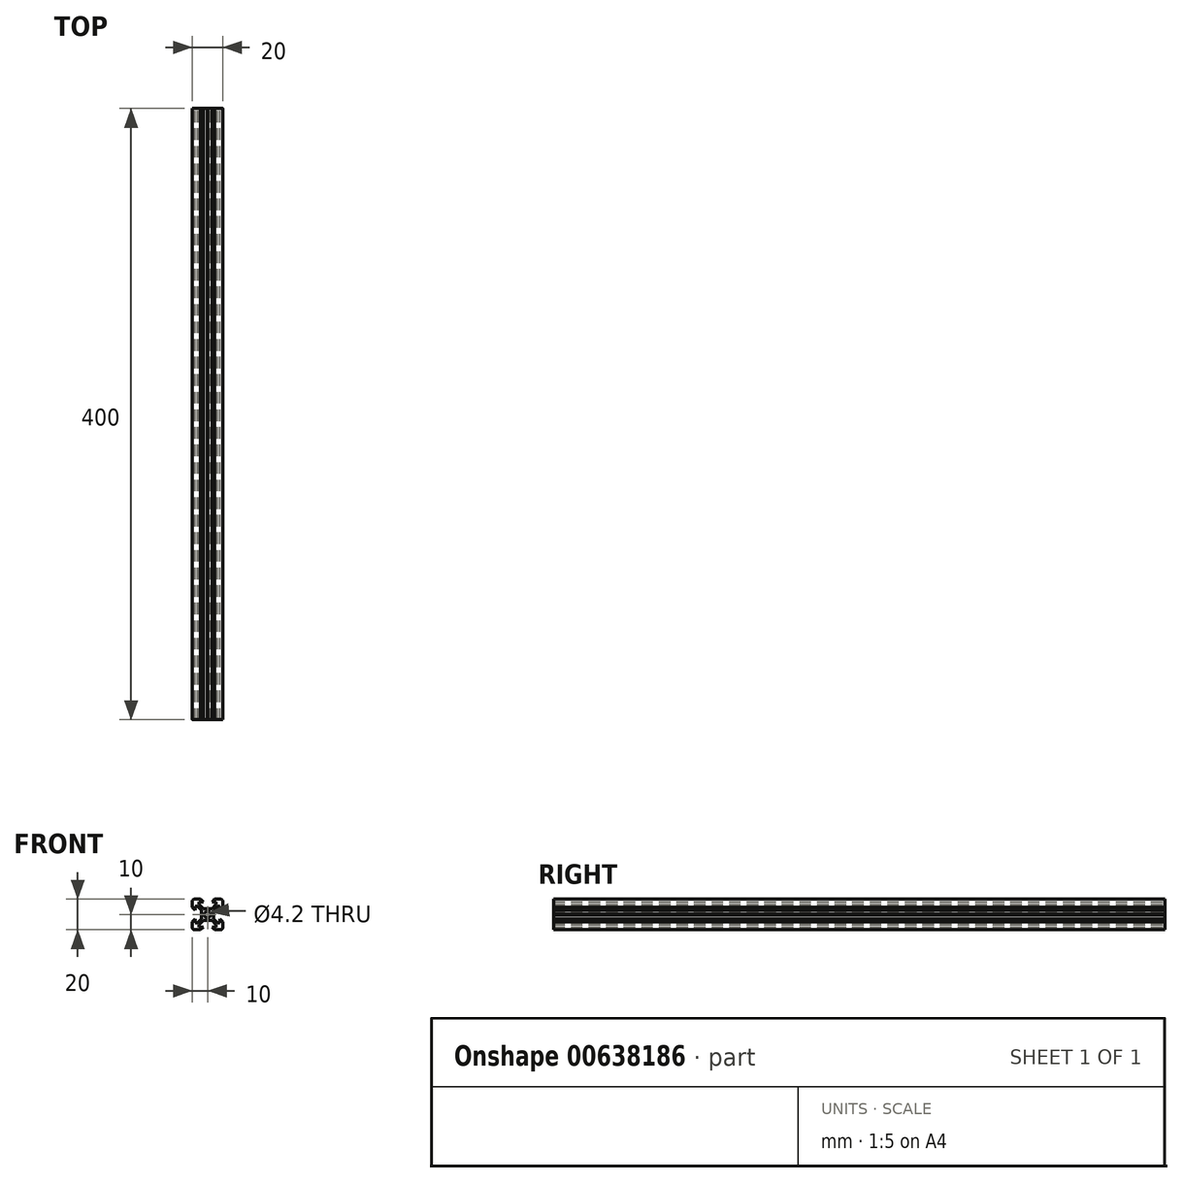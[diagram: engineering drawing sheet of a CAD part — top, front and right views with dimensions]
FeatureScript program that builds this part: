
annotation { "Feature Type Name" : "Feature", "Feature Type Description" : "" }
export const myFeature = defineFeature(function(context is Context, id is Id, definition is map)
    precondition{}
    {
        {
            var Q0;
            Q0=qCreatedBy(makeId("Front.planeOp"),FACE);
            var sketch = newSketch(context, id + "F0", { "sketchPlane" : qUnion([Q0])});
            skArc(sketch, "E0", {"start": v(-8.5, 10) * mm, "mid": v(-9.56, 9.56) * mm, "end": v(-10, 8.5) * mm});
            skLineSegment(sketch, "E1", {"start": v(-10, 8.5) * mm, "end": v(-10, 4.64) * mm});
            skLineSegment(sketch, "E2", {"start": v(-10, 4.64) * mm, "end": v(-8.2, 2.84) * mm});
            skLineSegment(sketch, "E3", {"start": v(-8.2, 5.5) * mm, "end": v(-8.2, 2.84) * mm});
            skLineSegment(sketch, "E4", {"start": v(-8.2, 5.5) * mm, "end": v(-6.56, 5.5) * mm});
            skLineSegment(sketch, "E5", {"start": v(-6.56, 5.5) * mm, "end": v(-3.9, 2.84) * mm});
            skLineSegment(sketch, "E6", {"start": v(-3.9, 2.84) * mm, "end": v(-3.9, 0.2) * mm});
            skLineSegment(sketch, "E7", {"start": v(-3.9, 0.2) * mm, "end": v(-3.7, 0) * mm});
            skLineSegment(sketch, "E8", {"start": v(-3.9, -0.2) * mm, "end": v(-3.7, 0) * mm});
            skLineSegment(sketch, "E9", {"start": v(-3.9, -2.84) * mm, "end": v(-3.9, -0.2) * mm});
            skLineSegment(sketch, "E10", {"start": v(-6.56, -5.5) * mm, "end": v(-3.9, -2.84) * mm});
            skLineSegment(sketch, "E11", {"start": v(-8.2, -5.5) * mm, "end": v(-6.56, -5.5) * mm});
            skLineSegment(sketch, "E12", {"start": v(-8.2, -5.5) * mm, "end": v(-8.2, -2.84) * mm});
            skLineSegment(sketch, "E13", {"start": v(-10, -4.64) * mm, "end": v(-8.2, -2.84) * mm});
            skLineSegment(sketch, "E14", {"start": v(-10, -8.5) * mm, "end": v(-10, -4.64) * mm});
            skArc(sketch, "E15", {"start": v(-10, -8.5) * mm, "mid": v(-9.56, -9.56) * mm, "end": v(-8.5, -10) * mm});
            skLineSegment(sketch, "E16", {"start": v(-8.5, -10) * mm, "end": v(-4.64, -10) * mm});
            skLineSegment(sketch, "E17", {"start": v(-4.64, -10) * mm, "end": v(-2.84, -8.2) * mm});
            skLineSegment(sketch, "E18", {"start": v(-2.84, -8.2) * mm, "end": v(-5.5, -8.2) * mm});
            skLineSegment(sketch, "E19", {"start": v(-5.5, -8.2) * mm, "end": v(-5.5, -6.56) * mm});
            skLineSegment(sketch, "E20", {"start": v(-5.5, -6.56) * mm, "end": v(-2.84, -3.9) * mm});
            skLineSegment(sketch, "E21", {"start": v(-0.2, -3.9) * mm, "end": v(-2.84, -3.9) * mm});
            skLineSegment(sketch, "E22", {"start": v(-0.2, -3.9) * mm, "end": v(0, -3.7) * mm});
            skLineSegment(sketch, "E23", {"start": v(0.2, -3.9) * mm, "end": v(0, -3.7) * mm});
            skLineSegment(sketch, "E24", {"start": v(0.2, -3.9) * mm, "end": v(2.84, -3.9) * mm});
            skLineSegment(sketch, "E25", {"start": v(5.5, -6.56) * mm, "end": v(2.84, -3.9) * mm});
            skLineSegment(sketch, "E26", {"start": v(5.5, -8.2) * mm, "end": v(5.5, -6.56) * mm});
            skLineSegment(sketch, "E27", {"start": v(2.84, -8.2) * mm, "end": v(5.5, -8.2) * mm});
            skLineSegment(sketch, "E28", {"start": v(4.64, -10) * mm, "end": v(2.84, -8.2) * mm});
            skLineSegment(sketch, "E29", {"start": v(8.5, -10) * mm, "end": v(4.64, -10) * mm});
            skArc(sketch, "E30", {"start": v(8.5, -10) * mm, "mid": v(9.56, -9.56) * mm, "end": v(10, -8.5) * mm});
            skLineSegment(sketch, "E31", {"start": v(10, -8.5) * mm, "end": v(10, -4.64) * mm});
            skLineSegment(sketch, "E32", {"start": v(10, -4.64) * mm, "end": v(8.2, -2.84) * mm});
            skLineSegment(sketch, "E33", {"start": v(8.2, -5.5) * mm, "end": v(8.2, -2.84) * mm});
            skLineSegment(sketch, "E34", {"start": v(8.2, -5.5) * mm, "end": v(6.56, -5.5) * mm});
            skLineSegment(sketch, "E35", {"start": v(6.56, -5.5) * mm, "end": v(3.9, -2.84) * mm});
            skLineSegment(sketch, "E36", {"start": v(3.9, -2.84) * mm, "end": v(3.9, -0.2) * mm});
            skLineSegment(sketch, "E37", {"start": v(3.9, -0.2) * mm, "end": v(3.7, 0) * mm});
            skLineSegment(sketch, "E38", {"start": v(3.9, 0.2) * mm, "end": v(3.7, 0) * mm});
            skLineSegment(sketch, "E39", {"start": v(3.9, 2.84) * mm, "end": v(3.9, 0.2) * mm});
            skLineSegment(sketch, "E40", {"start": v(6.56, 5.5) * mm, "end": v(3.9, 2.84) * mm});
            skLineSegment(sketch, "E41", {"start": v(8.2, 5.5) * mm, "end": v(6.56, 5.5) * mm});
            skLineSegment(sketch, "E42", {"start": v(8.2, 5.5) * mm, "end": v(8.2, 2.84) * mm});
            skLineSegment(sketch, "E43", {"start": v(10, 4.64) * mm, "end": v(8.2, 2.84) * mm});
            skLineSegment(sketch, "E44", {"start": v(10, 8.5) * mm, "end": v(10, 4.64) * mm});
            skArc(sketch, "E45", {"start": v(10, 8.5) * mm, "mid": v(9.56, 9.56) * mm, "end": v(8.5, 10) * mm});
            skLineSegment(sketch, "E46", {"start": v(8.5, 10) * mm, "end": v(4.64, 10) * mm});
            skLineSegment(sketch, "E47", {"start": v(4.64, 10) * mm, "end": v(2.84, 8.2) * mm});
            skLineSegment(sketch, "E48", {"start": v(2.84, 8.2) * mm, "end": v(5.5, 8.2) * mm});
            skLineSegment(sketch, "E49", {"start": v(5.5, 8.2) * mm, "end": v(5.5, 6.56) * mm});
            skLineSegment(sketch, "E50", {"start": v(5.5, 6.56) * mm, "end": v(2.84, 3.9) * mm});
            skLineSegment(sketch, "E51", {"start": v(0.2, 3.9) * mm, "end": v(2.84, 3.9) * mm});
            skLineSegment(sketch, "E52", {"start": v(0.2, 3.9) * mm, "end": v(0, 3.7) * mm});
            skLineSegment(sketch, "E53", {"start": v(-0.2, 3.9) * mm, "end": v(0, 3.7) * mm});
            skLineSegment(sketch, "E54", {"start": v(-0.2, 3.9) * mm, "end": v(-2.84, 3.9) * mm});
            skLineSegment(sketch, "E55", {"start": v(-5.5, 6.56) * mm, "end": v(-2.84, 3.9) * mm});
            skLineSegment(sketch, "E56", {"start": v(-5.5, 8.2) * mm, "end": v(-5.5, 6.56) * mm});
            skLineSegment(sketch, "E57", {"start": v(-2.84, 8.2) * mm, "end": v(-5.5, 8.2) * mm});
            skLineSegment(sketch, "E58", {"start": v(-4.64, 10) * mm, "end": v(-2.84, 8.2) * mm});
            skLineSegment(sketch, "E59", {"start": v(-8.5, 10) * mm, "end": v(-4.64, 10) * mm});
            skCircle(sketch, "E60", {"center": v(0, 0) * mm, "radius": 2.1 * mm});
            skSolve(sketch);
        }
        {
            var Q0;
            Q0 = qSketchRegion(id + "F0", true);
            extrude(context, id + "F1", {"entities" : qUnion([Q0]), "endBound" : BoundingType.SYMMETRIC, "depth" : 400 * mm, "offsetDistance" : 25.4 * mm});
        }
    });
